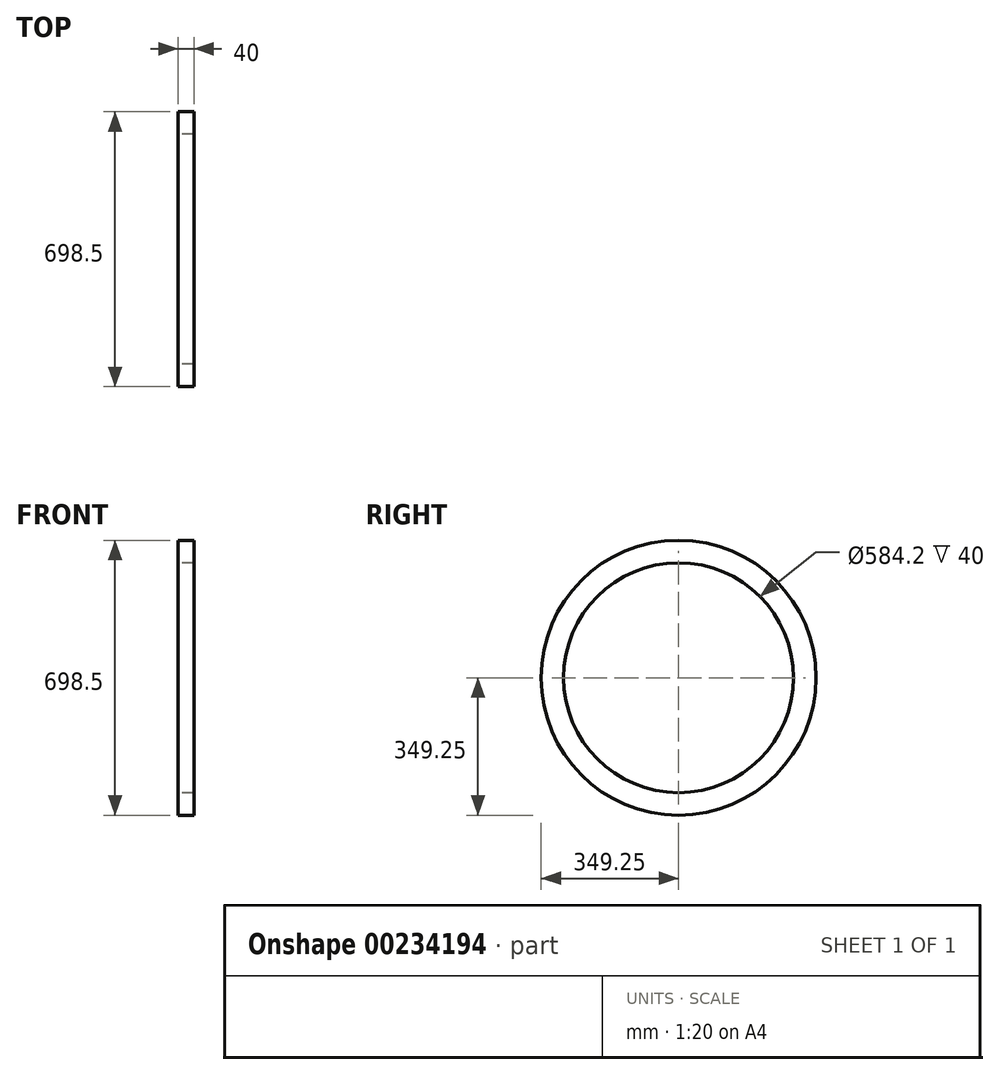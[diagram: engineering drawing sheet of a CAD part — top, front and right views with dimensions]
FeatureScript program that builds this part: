
annotation { "Feature Type Name" : "Feature", "Feature Type Description" : "" }
export const myFeature = defineFeature(function(context is Context, id is Id, definition is map)
    precondition{}
    {
        {
            var Q0;
            Q0=qCreatedBy(makeId("Right.planeOp"),FACE);
            var sketch = newSketch(context, id + "F0", { "sketchPlane" : qUnion([Q0])});
            skCircle(sketch, "E0", {"center": v(0, 0) * mm, "radius": 349.25 * mm});
            skCircle(sketch, "E1", {"center": v(0, 0) * mm, "radius": 292.1 * mm});
            skSolve(sketch);
        }
        {
            var Q0;
            Q0 = qSketchRegion(id + "F0", true);
            extrude(context, id + "F1", {"entities" : qUnion([Q0]), "endBound" : BoundingType.SYMMETRIC, "depth" : 40 * mm});
        }
    });
